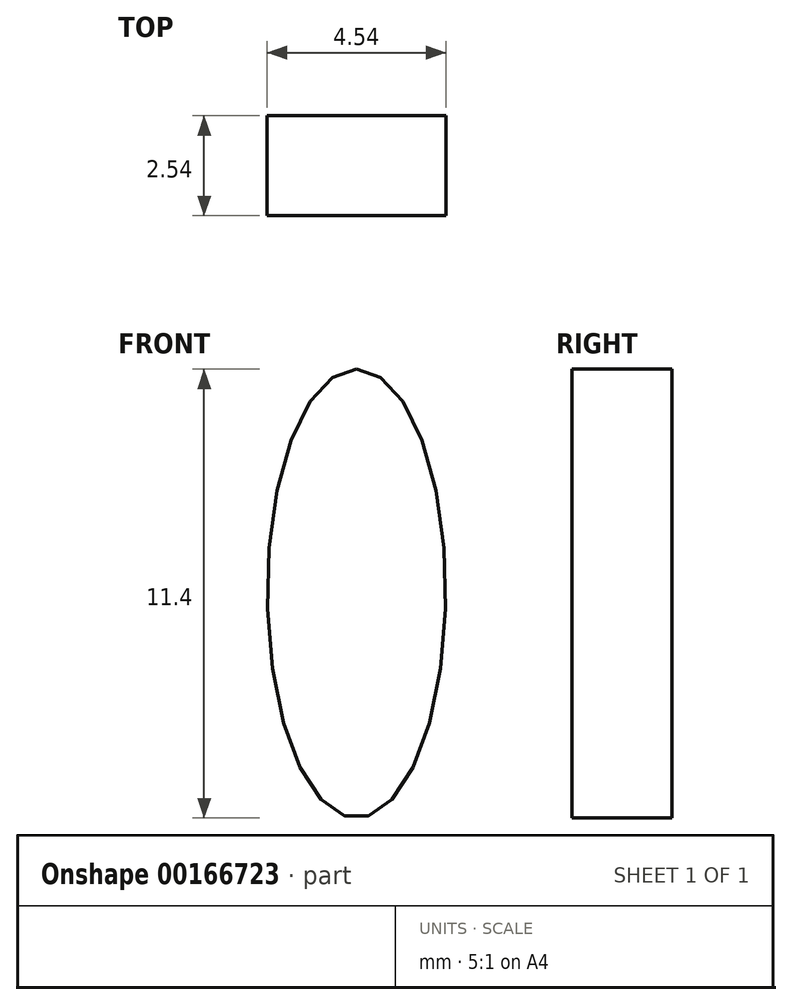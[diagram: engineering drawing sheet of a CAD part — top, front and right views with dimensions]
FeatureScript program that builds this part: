
annotation { "Feature Type Name" : "Feature", "Feature Type Description" : "" }
export const myFeature = defineFeature(function(context is Context, id is Id, definition is map)
    precondition{}
    {
        {
            var Q0;
            Q0=qCreatedBy(makeId("Front.planeOp"),FACE);
            var sketch = newSketch(context, id + "F0", { "sketchPlane" : qUnion([Q0])});
            skEllipse(sketch, "E0", {"center": v(0, 0) * mm, "majorRadius": 5.7 * mm, "minorRadius": 2.27 * mm, "majorAxis": v(0, 1)});
            skSolve(sketch);
        }
        {
            var Q0;
            Q0 = qSketchRegion(id + "F0", true);
            extrude(context, id + "F1", {"entities" : qUnion([Q0]), "depth" : 2.54 * mm});
        }
    });
